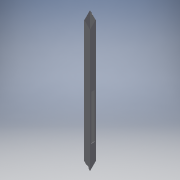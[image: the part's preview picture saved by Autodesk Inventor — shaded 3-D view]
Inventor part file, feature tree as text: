
AUTODESK INVENTOR PART (.ipt)
format: ipt  version: 2016 (Build 200138000, 138)  size: 130,048 bytes
history: native  units: in
note: dims shown in document units (in); Inventor stores cm internally (conversion verified against a paired STEP export)
features: extrude x4, sketch x4
ambient origin geometry x8: Origin, YZ Plane, XZ Plane, XY Plane, X Axis, Y Axis, Z Axis, Center Point
bodies: Solid1 (feature_tree)
feature tree (8):
  extrude  "Extrusion1"  Depth=1.0in
  extrude  "Extrusion2"  Depth=22.75in TaperAngle=0.0deg
  extrude  "Extrusion4"  Depth=0.5in
  extrude  "Extrusion5"  Depth=7.5in
  sketch  "Sketch1"  dims[d0=1.0in d1=1.0in]
  sketch  "Sketch2"  dims[d2=0.0625in d3=22.75in d4=0.0in]
  sketch  "Sketch4"  dims[d5=0.5in d6=0.5in]
  sketch  "Sketch5"  dims[d7=1.0in d8=0.0in d14=0.5in d15=0.518in d16=0.5in d17=1.0in d18=0.0in d19=0.2in d20=0.2in d21=4.0in d22=1.0in d23=0.0in d24=7.5in]
